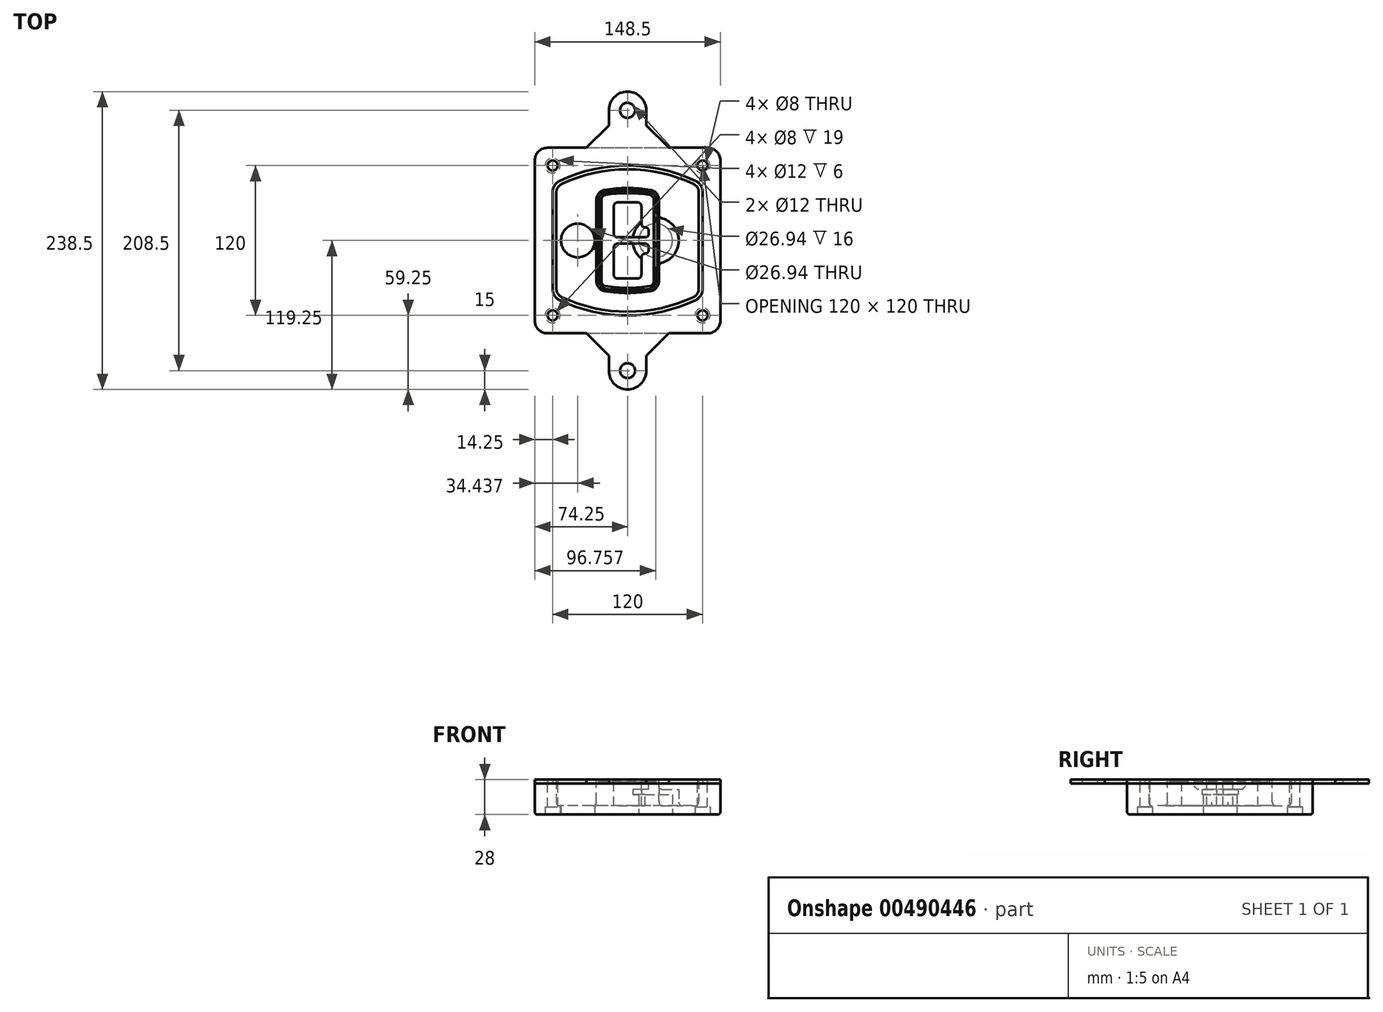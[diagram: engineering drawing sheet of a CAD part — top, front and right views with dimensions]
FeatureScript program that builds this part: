
annotation { "Feature Type Name" : "Feature", "Feature Type Description" : "" }
export const myFeature = defineFeature(function(context is Context, id is Id, definition is map)
    precondition{}
    {
        {
            var Q0;
            Q0=qCreatedBy(makeId("Top.planeOp"),FACE);
            var sketch = newSketch(context, id + "F0", { "sketchPlane" : qUnion([Q0])});
            skPoint(sketch, "E0.rect.middle", {"position": v(0, 0) * mm});
            skLineSegment(sketch, "E1.bottom", {"start": v(-64.25, -74.25) * mm, "end": v(64.25, -74.25) * mm});
            skLineSegment(sketch, "E1.top", {"start": v(-64.25, 74.25) * mm, "end": v(64.25, 74.25) * mm});
            skLineSegment(sketch, "E1.left", {"start": v(-74.25, -64.25) * mm, "end": v(-74.25, 64.25) * mm});
            skLineSegment(sketch, "E1.right", {"start": v(74.25, -64.25) * mm, "end": v(74.25, 64.25) * mm});
            skLineSegment(sketch, "E2", {"start": v(-74.25, 74.25) * mm, "end": v(74.25, -74.25) * mm, "construction": true});
            skLineSegment(sketch, "E3", {"start": v(74.25, 74.25) * mm, "end": v(-74.25, -74.25) * mm, "construction": true});
            skCircle(sketch, "E4", {"center": v(-60, 60) * mm, "radius": 4 * mm});
            skCircle(sketch, "E5", {"center": v(60, 60) * mm, "radius": 4 * mm});
            skCircle(sketch, "E6", {"center": v(60, -60) * mm, "radius": 4 * mm});
            skCircle(sketch, "E7", {"center": v(-60, -60) * mm, "radius": 4 * mm});
            skLineSegment(sketch, "E8", {"start": v(-60, 60) * mm, "end": v(60, 60) * mm, "construction": true});
            skLineSegment(sketch, "E9", {"start": v(60, 60) * mm, "end": v(60, -60) * mm, "construction": true});
            skLineSegment(sketch, "E10", {"start": v(60, -60) * mm, "end": v(-60, -60) * mm, "construction": true});
            skLineSegment(sketch, "E11", {"start": v(-60, -60) * mm, "end": v(-60, 60) * mm, "construction": true});
            skLineSegment(sketch, "E12", {"start": v(-60, 38.83) * mm, "end": v(-60, -38.83) * mm});
            skLineSegment(sketch, "E13", {"start": v(60, 38.83) * mm, "end": v(60, -38.83) * mm});
            skArc(sketch, "E14", {"start": v(54.26, 47.88) * mm, "mid": v(0, 60) * mm, "end": v(-54.26, 47.88) * mm});
            skArc(sketch, "E15", {"start": v(-54.26, -47.88) * mm, "mid": v(0, -60) * mm, "end": v(54.26, -47.88) * mm});
            skLineSegment(sketch, "E16", {"start": v(-60, 0) * mm, "end": v(60, 0) * mm, "construction": true});
            skPoint(sketch, "E17.visualSharp", {"position": v(-60, -45) * mm});
            skArc(sketch, "E17.filletArc", {"start": v(-60, -38.83) * mm, "mid": v(-58.44, -44.2) * mm, "end": v(-54.26, -47.88) * mm});
            skPoint(sketch, "E18.visualSharp", {"position": v(-60, 45) * mm});
            skArc(sketch, "E18.filletArc", {"start": v(-54.26, 47.88) * mm, "mid": v(-58.44, 44.2) * mm, "end": v(-60, 38.83) * mm});
            skPoint(sketch, "E19.visualSharp", {"position": v(60, 45) * mm});
            skArc(sketch, "E19.filletArc", {"start": v(60, 38.83) * mm, "mid": v(58.44, 44.2) * mm, "end": v(54.26, 47.88) * mm});
            skPoint(sketch, "E20.visualSharp", {"position": v(60, -45) * mm});
            skArc(sketch, "E20.filletArc", {"start": v(54.26, -47.88) * mm, "mid": v(58.44, -44.2) * mm, "end": v(60, -38.83) * mm});
            skPoint(sketch, "E21.visualSharp", {"position": v(-74.25, 74.25) * mm});
            skArc(sketch, "E21.filletArc", {"start": v(-64.25, 74.25) * mm, "mid": v(-71.32, 71.32) * mm, "end": v(-74.25, 64.25) * mm});
            skPoint(sketch, "E22.visualSharp", {"position": v(74.25, 74.25) * mm});
            skArc(sketch, "E22.filletArc", {"start": v(74.25, 64.25) * mm, "mid": v(71.32, 71.32) * mm, "end": v(64.25, 74.25) * mm});
            skPoint(sketch, "E23.visualSharp", {"position": v(74.25, -74.25) * mm});
            skArc(sketch, "E23.filletArc", {"start": v(64.25, -74.25) * mm, "mid": v(71.32, -71.32) * mm, "end": v(74.25, -64.25) * mm});
            skPoint(sketch, "E24.visualSharp", {"position": v(-74.25, -74.25) * mm});
            skArc(sketch, "E24.filletArc", {"start": v(-74.25, -64.25) * mm, "mid": v(-71.32, -71.32) * mm, "end": v(-64.25, -74.25) * mm});
            skArc(sketch, "E25.0", {"start": v(57, 38.83) * mm, "mid": v(55.9, 42.58) * mm, "end": v(52.98, 45.17) * mm});
            skLineSegment(sketch, "E25.1", {"start": v(57, 38.83) * mm, "end": v(57, -38.83) * mm});
            skArc(sketch, "E25.2", {"start": v(52.98, -45.17) * mm, "mid": v(55.9, -42.58) * mm, "end": v(57, -38.83) * mm});
            skArc(sketch, "E25.3", {"start": v(-52.98, -45.17) * mm, "mid": v(0, -57) * mm, "end": v(52.98, -45.17) * mm});
            skArc(sketch, "E25.4", {"start": v(-57, -38.83) * mm, "mid": v(-55.9, -42.58) * mm, "end": v(-52.98, -45.17) * mm});
            skArc(sketch, "E25.5", {"start": v(52.98, 45.17) * mm, "mid": v(0, 57) * mm, "end": v(-52.98, 45.17) * mm});
            skLineSegment(sketch, "E25.6", {"start": v(-57, 38.83) * mm, "end": v(-57, -38.83) * mm});
            skArc(sketch, "E25.7", {"start": v(-52.98, 45.17) * mm, "mid": v(-55.9, 42.58) * mm, "end": v(-57, 38.83) * mm});
            skArc(sketch, "E26.0", {"start": v(-55.96, 51.5) * mm, "mid": v(-61.82, 46.33) * mm, "end": v(-64, 38.83) * mm});
            skArc(sketch, "E26.1", {"start": v(55.96, 51.5) * mm, "mid": v(0, 64) * mm, "end": v(-55.96, 51.5) * mm});
            skArc(sketch, "E26.2", {"start": v(64, 38.83) * mm, "mid": v(61.82, 46.33) * mm, "end": v(55.96, 51.5) * mm});
            skLineSegment(sketch, "E26.3", {"start": v(64, 38.83) * mm, "end": v(64, -38.83) * mm});
            skArc(sketch, "E26.4", {"start": v(55.96, -51.5) * mm, "mid": v(61.82, -46.33) * mm, "end": v(64, -38.83) * mm});
            skLineSegment(sketch, "E26.5", {"start": v(-64, 38.83) * mm, "end": v(-64, -38.83) * mm});
            skArc(sketch, "E26.6", {"start": v(-55.96, -51.5) * mm, "mid": v(0, -64) * mm, "end": v(55.96, -51.5) * mm});
            skArc(sketch, "E26.7", {"start": v(-64, -38.83) * mm, "mid": v(-61.82, -46.33) * mm, "end": v(-55.96, -51.5) * mm});
            skSolve(sketch);
        }
        {
            var Q0;
            Q0=makeQuery(id+"F0.imprint","IMPRINT",FACE,{"disambiguationData":[TD([[makeQuery(id+"F0.imprint","IMPRINT",EDGE,{"derivedFrom":sQuery(id+"F0.wireOp",EDGE,"E1.bottom")}),1.0]])]});
            var Q1;
            Q1=makeQuery(id+"F0.imprint","IMPRINT",FACE,{"disambiguationData":[TD([[makeQuery(id+"F0.imprint","IMPRINT",EDGE,{"derivedFrom":sQuery(id+"F0.wireOp",EDGE,"E12")}),1.0]])]});
            var Q2;
            Q2=makeQuery(id+"F0.imprint","IMPRINT",FACE,{"disambiguationData":[TD([[makeQuery(id+"F0.imprint","IMPRINT",EDGE,{"derivedFrom":sQuery(id+"F0.wireOp",EDGE,"E25.0")}),1.0]])]});
            var Q3;
            Q3=makeQuery(id+"F0.imprint","IMPRINT",FACE,{"disambiguationData":[TD([[makeQuery(id+"F0.imprint","IMPRINT",EDGE,{"derivedFrom":sQuery(id+"F0.wireOp",EDGE,"E12")}),-1.0]])]});
            extrude(context, id + "F1", {"entities" : qUnion([Q0, Q1, Q2, Q3]), "oppositeDirection" : true, "depth" : 25 * mm});
        }
        {
            var Q0;
            Q0=makeQuery(id+"F0.imprint","IMPRINT",FACE,{"disambiguationData":[TD([[makeQuery(id+"F0.imprint","IMPRINT",EDGE,{"derivedFrom":sQuery(id+"F0.wireOp",EDGE,"E12")}),1.0]])]});
            extrude(context, id + "F2", {"entities" : qUnion([Q0]), "operationType" : NewBodyOperationType.ADD, "depth" : 3 * mm});
        }
        {
            var Q0;
            Q0=makeQuery(id+"F0.imprint","IMPRINT",FACE,{"disambiguationData":[TD([[makeQuery(id+"F0.imprint","IMPRINT",EDGE,{"derivedFrom":sQuery(id+"F0.wireOp",EDGE,"E25.0")}),1.0]])]});
            extrude(context, id + "F3", {"entities" : qUnion([Q0]), "operationType" : NewBodyOperationType.REMOVE, "oppositeDirection" : true, "depth" : 18 * mm});
        }
        {
            var Q0;
            Q0=makeQuery(id+"F2.opExtrude","CAP_FACE",FACE,{"disambiguationData":[OSD([sQuery(id+"F0.wireOp",EDGE,"E12"),sQuery(id+"F0.wireOp",EDGE,"E13"),sQuery(id+"F0.wireOp",EDGE,"E14"),sQuery(id+"F0.wireOp",EDGE,"E15"),sQuery(id+"F0.wireOp",EDGE,"E17.filletArc"),sQuery(id+"F0.wireOp",EDGE,"E18.filletArc"),sQuery(id+"F0.wireOp",EDGE,"E19.filletArc"),sQuery(id+"F0.wireOp",EDGE,"E20.filletArc"),sQuery(id+"F0.wireOp",EDGE,"E25.0"),sQuery(id+"F0.wireOp",EDGE,"E25.1"),sQuery(id+"F0.wireOp",EDGE,"E25.2"),sQuery(id+"F0.wireOp",EDGE,"E25.3"),sQuery(id+"F0.wireOp",EDGE,"E25.4"),sQuery(id+"F0.wireOp",EDGE,"E25.5"),sQuery(id+"F0.wireOp",EDGE,"E25.6"),sQuery(id+"F0.wireOp",EDGE,"E25.7")])],"isStart":false});
            var sketch = newSketch(context, id + "F4", { "sketchPlane" : qUnion([Q0])});
            skArc(sketch, "E27.0", {"start": v(-18.34, -40.45) * mm, "mid": v(0, -42) * mm, "end": v(18.34, -40.45) * mm});
            skArc(sketch, "E28.0", {"start": v(18.34, 40.45) * mm, "mid": v(0, 42) * mm, "end": v(-18.34, 40.45) * mm});
            skLineSegment(sketch, "E29", {"start": v(-25, 32.57) * mm, "end": v(-25, -32.57) * mm});
            skLineSegment(sketch, "E30", {"start": v(25, 32.57) * mm, "end": v(25, -32.57) * mm});
            skLineSegment(sketch, "E31", {"start": v(-25, 39.1) * mm, "end": v(25, 39.1) * mm, "construction": true});
            skLineSegment(sketch, "E32", {"start": v(-25, -39.1) * mm, "end": v(25, -39.1) * mm, "construction": true});
            skPoint(sketch, "E33.visualSharp", {"position": v(-25, 39.1) * mm});
            skArc(sketch, "E33.filletArc", {"start": v(-18.34, 40.45) * mm, "mid": v(-23.11, 37.73) * mm, "end": v(-25, 32.57) * mm});
            skPoint(sketch, "E34.visualSharp", {"position": v(25, 39.1) * mm});
            skArc(sketch, "E34.filletArc", {"start": v(25, 32.57) * mm, "mid": v(23.11, 37.73) * mm, "end": v(18.34, 40.45) * mm});
            skPoint(sketch, "E35.visualSharp", {"position": v(25, -39.1) * mm});
            skArc(sketch, "E35.filletArc", {"start": v(18.34, -40.45) * mm, "mid": v(23.11, -37.73) * mm, "end": v(25, -32.57) * mm});
            skPoint(sketch, "E36.visualSharp", {"position": v(-25, -39.1) * mm});
            skArc(sketch, "E36.filletArc", {"start": v(-25, -32.57) * mm, "mid": v(-23.11, -37.73) * mm, "end": v(-18.34, -40.45) * mm});
            skArc(sketch, "E37.0", {"start": v(52.98, 45.17) * mm, "mid": v(0, 57) * mm, "end": v(-52.98, 45.17) * mm});
            skArc(sketch, "E37.1", {"start": v(-52.98, 45.17) * mm, "mid": v(-55.9, 42.58) * mm, "end": v(-57, 38.83) * mm});
            skLineSegment(sketch, "E37.2", {"start": v(-57, 38.83) * mm, "end": v(-57, -38.83) * mm});
            skArc(sketch, "E37.3", {"start": v(-57, -38.83) * mm, "mid": v(-55.9, -42.58) * mm, "end": v(-52.98, -45.17) * mm});
            skArc(sketch, "E37.4", {"start": v(-52.98, -45.17) * mm, "mid": v(0, -57) * mm, "end": v(52.98, -45.17) * mm});
            skArc(sketch, "E37.5", {"start": v(52.98, -45.17) * mm, "mid": v(55.9, -42.58) * mm, "end": v(57, -38.83) * mm});
            skLineSegment(sketch, "E37.6", {"start": v(57, 38.83) * mm, "end": v(57, -38.83) * mm});
            skArc(sketch, "E37.7", {"start": v(57, 38.83) * mm, "mid": v(55.9, 42.58) * mm, "end": v(52.98, 45.17) * mm});
            skLineSegment(sketch, "E38.0", {"start": v(23, 32.57) * mm, "end": v(23, -32.57) * mm});
            skArc(sketch, "E38.1", {"start": v(18, -38.48) * mm, "mid": v(21.58, -36.44) * mm, "end": v(23, -32.57) * mm});
            skArc(sketch, "E38.2", {"start": v(-18, -38.48) * mm, "mid": v(0, -40) * mm, "end": v(18, -38.48) * mm});
            skArc(sketch, "E38.3", {"start": v(-23, -32.57) * mm, "mid": v(-21.58, -36.44) * mm, "end": v(-18, -38.48) * mm});
            skLineSegment(sketch, "E38.4", {"start": v(-23, 32.57) * mm, "end": v(-23, -32.57) * mm});
            skArc(sketch, "E38.5", {"start": v(23, 32.57) * mm, "mid": v(21.58, 36.44) * mm, "end": v(18, 38.48) * mm});
            skArc(sketch, "E38.6", {"start": v(-18, 38.48) * mm, "mid": v(-21.58, 36.44) * mm, "end": v(-23, 32.57) * mm});
            skArc(sketch, "E38.7", {"start": v(18, 38.48) * mm, "mid": v(0, 40) * mm, "end": v(-18, 38.48) * mm});
            skArc(sketch, "E39.0", {"start": v(21, 32.57) * mm, "mid": v(20.06, 35.15) * mm, "end": v(17.67, 36.5) * mm});
            skLineSegment(sketch, "E39.1", {"start": v(21, 32.57) * mm, "end": v(21, -32.57) * mm});
            skArc(sketch, "E39.2", {"start": v(17.67, -36.5) * mm, "mid": v(20.06, -35.15) * mm, "end": v(21, -32.57) * mm});
            skArc(sketch, "E39.3", {"start": v(-17.67, -36.5) * mm, "mid": v(0, -38) * mm, "end": v(17.67, -36.5) * mm});
            skArc(sketch, "E39.4", {"start": v(-21, -32.57) * mm, "mid": v(-20.06, -35.15) * mm, "end": v(-17.67, -36.5) * mm});
            skArc(sketch, "E39.5", {"start": v(17.67, 36.5) * mm, "mid": v(0, 38) * mm, "end": v(-17.67, 36.5) * mm});
            skLineSegment(sketch, "E39.6", {"start": v(-21, 32.57) * mm, "end": v(-21, -32.57) * mm});
            skArc(sketch, "E39.7", {"start": v(-17.67, 36.5) * mm, "mid": v(-20.06, 35.15) * mm, "end": v(-21, 32.57) * mm});
            skLineSegment(sketch, "E40", {"start": v(-25, 0) * mm, "end": v(25, 0) * mm, "construction": true});
            skLineSegment(sketch, "E41", {"start": v(-11, 5.5) * mm, "end": v(-11, 27.5) * mm});
            skLineSegment(sketch, "E42", {"start": v(-8, 30.5) * mm, "end": v(8, 30.5) * mm});
            skLineSegment(sketch, "E43", {"start": v(11, 27.5) * mm, "end": v(11, 13.5) * mm});
            skLineSegment(sketch, "E44", {"start": v(14, 10.5) * mm, "end": v(14, 10.5) * mm});
            skLineSegment(sketch, "E45", {"start": v(17, 7.5) * mm, "end": v(17, 5.5) * mm});
            skLineSegment(sketch, "E46", {"start": v(14, 2.5) * mm, "end": v(-8, 2.5) * mm});
            skPoint(sketch, "E47.visualSharp", {"position": v(-11, 30.5) * mm});
            skArc(sketch, "E47.filletArc", {"start": v(-8, 30.5) * mm, "mid": v(-10.12, 29.62) * mm, "end": v(-11, 27.5) * mm});
            skPoint(sketch, "E48.visualSharp", {"position": v(11, 30.5) * mm});
            skArc(sketch, "E48.filletArc", {"start": v(11, 27.5) * mm, "mid": v(10.12, 29.62) * mm, "end": v(8, 30.5) * mm});
            skPoint(sketch, "E49.visualSharp", {"position": v(11, 10.5) * mm});
            skArc(sketch, "E49.filletArc", {"start": v(11, 13.5) * mm, "mid": v(11.88, 11.38) * mm, "end": v(14, 10.5) * mm});
            skPoint(sketch, "E50.visualSharp", {"position": v(17, 10.5) * mm});
            skArc(sketch, "E50.filletArc", {"start": v(17, 7.5) * mm, "mid": v(16.12, 9.62) * mm, "end": v(14, 10.5) * mm});
            skPoint(sketch, "E51.visualSharp", {"position": v(17, 2.5) * mm});
            skArc(sketch, "E51.filletArc", {"start": v(14, 2.5) * mm, "mid": v(16.12, 3.38) * mm, "end": v(17, 5.5) * mm});
            skPoint(sketch, "E52.visualSharp", {"position": v(-11, 2.5) * mm});
            skArc(sketch, "E52.filletArc", {"start": v(-11, 5.5) * mm, "mid": v(-10.12, 3.38) * mm, "end": v(-8, 2.5) * mm});
            skLineSegment(sketch, "E53.0.MirrorCS", {"start": v(14, -2.5) * mm, "end": v(-8, -2.5) * mm});
            skArc(sketch, "E54.0.MirrorCS", {"start": v(-11, -5.5) * mm, "mid": v(-10.12, -3.38) * mm, "end": v(-8, -2.5) * mm});
            skLineSegment(sketch, "E55.0.MirrorCS", {"start": v(-11, -5.5) * mm, "end": v(-11, -27.5) * mm});
            skArc(sketch, "E56.0.MirrorCS", {"start": v(-8, -30.5) * mm, "mid": v(-10.12, -29.62) * mm, "end": v(-11, -27.5) * mm});
            skLineSegment(sketch, "E57.0.MirrorCS", {"start": v(-8, -30.5) * mm, "end": v(8, -30.5) * mm});
            skArc(sketch, "E58.0.MirrorCS", {"start": v(11, -27.5) * mm, "mid": v(10.12, -29.62) * mm, "end": v(8, -30.5) * mm});
            skLineSegment(sketch, "E59.0.MirrorCS", {"start": v(11, -27.5) * mm, "end": v(11, -13.5) * mm});
            skArc(sketch, "E60.0.MirrorCS", {"start": v(11, -13.5) * mm, "mid": v(11.88, -11.38) * mm, "end": v(14, -10.5) * mm});
            skArc(sketch, "E61.0.MirrorCS", {"start": v(17, -7.5) * mm, "mid": v(16.12, -9.62) * mm, "end": v(14, -10.5) * mm});
            skLineSegment(sketch, "E62.0.MirrorCS", {"start": v(17, -7.5) * mm, "end": v(17, -5.5) * mm});
            skArc(sketch, "E63.0.MirrorCS", {"start": v(14, -2.5) * mm, "mid": v(16.12, -3.38) * mm, "end": v(17, -5.5) * mm});
            skSolve(sketch);
        }
        {
            var Q0;
            Q0=makeQuery(id+"F4.imprint","IMPRINT",FACE,{"disambiguationData":[TD([[makeQuery(id+"F4.imprint","IMPRINT",EDGE,{"derivedFrom":sQuery(id+"F4.wireOp",EDGE,"E27.0")}),1.0]])]});
            var Q1;
            Q1=makeQuery(id+"F4.imprint","IMPRINT",FACE,{"disambiguationData":[TD([[makeQuery(id+"F4.imprint","IMPRINT",EDGE,{"derivedFrom":sQuery(id+"F4.wireOp",EDGE,"E38.0")}),-1.0]])]});
            var Q2;
            Q2=makeQuery(id+"F4.imprint","IMPRINT",FACE,{"disambiguationData":[TD([[makeQuery(id+"F4.imprint","IMPRINT",EDGE,{"derivedFrom":sQuery(id+"F4.wireOp",EDGE,"E39.0")}),1.0]])]});
            extrude(context, id + "F5", {"entities" : qUnion([Q0, Q1, Q2]), "operationType" : NewBodyOperationType.ADD, "endBound" : BoundingType.UP_TO_NEXT, "oppositeDirection" : true, "depth" : 25 * mm});
        }
        {
            var Q0;
            Q0=makeQuery(id+"F4.imprint","IMPRINT",FACE,{"disambiguationData":[TD([[makeQuery(id+"F4.imprint","IMPRINT",EDGE,{"derivedFrom":sQuery(id+"F4.wireOp",EDGE,"E38.0")}),-1.0]])]});
            extrude(context, id + "F6", {"entities" : qUnion([Q0]), "operationType" : NewBodyOperationType.REMOVE, "oppositeDirection" : true, "depth" : 2 * mm});
        }
        {
            var Q0;
            Q0=makeQuery(id+"F1.opExtrude","CAP_FACE",FACE,{"disambiguationData":[OSD([sQuery(id+"F0.wireOp",EDGE,"E1.bottom"),sQuery(id+"F0.wireOp",EDGE,"E1.top"),sQuery(id+"F0.wireOp",EDGE,"E1.left"),sQuery(id+"F0.wireOp",EDGE,"E1.right"),sQuery(id+"F0.wireOp",EDGE,"E4"),sQuery(id+"F0.wireOp",EDGE,"E5"),sQuery(id+"F0.wireOp",EDGE,"E6"),sQuery(id+"F0.wireOp",EDGE,"E7"),sQuery(id+"F0.wireOp",EDGE,"E21.filletArc"),sQuery(id+"F0.wireOp",EDGE,"E22.filletArc"),sQuery(id+"F0.wireOp",EDGE,"E23.filletArc"),sQuery(id+"F0.wireOp",EDGE,"E24.filletArc")])],"isStart":false});
            var sketch = newSketch(context, id + "F7", { "sketchPlane" : qUnion([Q0])});
            skCircle(sketch, "E64", {"center": v(22.5, 0) * mm, "radius": 13.47 * mm});
            skCircle(sketch, "E65", {"center": v(-39.81, 0) * mm, "radius": 13.47 * mm});
            skLineSegment(sketch, "E66", {"start": v(74.25, 0) * mm, "end": v(-74.25, 0) * mm});
            skCircle(sketch, "E67", {"center": v(22.5, 0) * mm, "radius": 18.47 * mm});
            skCircle(sketch, "E68", {"center": v(60, -60) * mm, "radius": 6 * mm});
            skCircle(sketch, "E69", {"center": v(-60, -60) * mm, "radius": 6 * mm});
            skCircle(sketch, "E70", {"center": v(-60, 60) * mm, "radius": 6 * mm});
            skCircle(sketch, "E71", {"center": v(60, 60) * mm, "radius": 6 * mm});
            skSolve(sketch);
        }
        {
            var Q0;
            {var subQ1=sQuery(id+"F7.wireOp",EDGE,"E66");var subQ4=sQuery(id+"F7.wireOp",EDGE,"E64");var subQ6=makeQuery(id+"F7.imprint","INTERSECT",VERTEX,{"disambiguationData":[OD(0.0)],"derivedFrom":[subQ4,subQ1]});Q0=makeQuery(id+"F7.imprint","IMPRINT",FACE,{"disambiguationData":[TD([[makeQuery(id+"F7.imprint","IMPRINT",EDGE,{"disambiguationData":[TD([[subQ6,-1.0]])],"derivedFrom":subQ4}),-1.0]])]});}
            var Q1;
            {var subQ0=sQuery(id+"F7.wireOp",EDGE,"E66");var subQ1=sQuery(id+"F7.wireOp",EDGE,"E64");var subQ3=makeQuery(id+"F7.imprint","INTERSECT",VERTEX,{"disambiguationData":[OD(0.0)],"derivedFrom":[subQ1,subQ0]});Q1=makeQuery(id+"F7.imprint","IMPRINT",FACE,{"disambiguationData":[TD([[makeQuery(id+"F7.imprint","IMPRINT",EDGE,{"disambiguationData":[TD([[subQ3,-1.0]])],"derivedFrom":subQ1}),1.0]])]});}
            var Q2;
            {var subQ0=sQuery(id+"F7.wireOp",EDGE,"E66");var subQ1=sQuery(id+"F7.wireOp",EDGE,"E64");var subQ3=makeQuery(id+"F7.imprint","INTERSECT",VERTEX,{"disambiguationData":[OD(0.0)],"derivedFrom":[subQ1,subQ0]});Q2=makeQuery(id+"F7.imprint","IMPRINT",FACE,{"disambiguationData":[TD([[makeQuery(id+"F7.imprint","IMPRINT",EDGE,{"disambiguationData":[TD([[subQ3,1.0]])],"derivedFrom":subQ1}),1.0]])]});}
            var Q3;
            {var subQ1=sQuery(id+"F7.wireOp",EDGE,"E66");var subQ4=sQuery(id+"F7.wireOp",EDGE,"E64");var subQ6=makeQuery(id+"F7.imprint","INTERSECT",VERTEX,{"disambiguationData":[OD(0.0)],"derivedFrom":[subQ4,subQ1]});Q3=makeQuery(id+"F7.imprint","IMPRINT",FACE,{"disambiguationData":[TD([[makeQuery(id+"F7.imprint","IMPRINT",EDGE,{"disambiguationData":[TD([[subQ6,1.0]])],"derivedFrom":subQ4}),-1.0]])]});}
            extrude(context, id + "F8", {"entities" : qUnion([Q0, Q1, Q2, Q3]), "operationType" : NewBodyOperationType.ADD, "oppositeDirection" : true, "depth" : 20 * mm});
        }
        {
            var Q0;
            {var subQ0=sQuery(id+"F7.wireOp",EDGE,"E66");var subQ1=sQuery(id+"F7.wireOp",EDGE,"E64");var subQ3=makeQuery(id+"F7.imprint","INTERSECT",VERTEX,{"disambiguationData":[OD(0.0)],"derivedFrom":[subQ1,subQ0]});Q0=makeQuery(id+"F7.imprint","IMPRINT",FACE,{"disambiguationData":[TD([[makeQuery(id+"F7.imprint","IMPRINT",EDGE,{"disambiguationData":[TD([[subQ3,-1.0]])],"derivedFrom":subQ1}),1.0]])]});}
            var Q1;
            {var subQ0=sQuery(id+"F7.wireOp",EDGE,"E66");var subQ1=sQuery(id+"F7.wireOp",EDGE,"E64");var subQ3=makeQuery(id+"F7.imprint","INTERSECT",VERTEX,{"disambiguationData":[OD(0.0)],"derivedFrom":[subQ1,subQ0]});Q1=makeQuery(id+"F7.imprint","IMPRINT",FACE,{"disambiguationData":[TD([[makeQuery(id+"F7.imprint","IMPRINT",EDGE,{"disambiguationData":[TD([[subQ3,1.0]])],"derivedFrom":subQ1}),1.0]])]});}
            extrude(context, id + "F9", {"entities" : qUnion([Q0, Q1]), "operationType" : NewBodyOperationType.REMOVE, "oppositeDirection" : true, "depth" : 16 * mm});
        }
        {
            var Q0;
            {var subQ0=sQuery(id+"F7.wireOp",EDGE,"E66");var subQ1=sQuery(id+"F7.wireOp",EDGE,"E65");var subQ3=makeQuery(id+"F7.imprint","INTERSECT",VERTEX,{"disambiguationData":[OD(0.0)],"derivedFrom":[subQ1,subQ0]});Q0=makeQuery(id+"F7.imprint","IMPRINT",FACE,{"disambiguationData":[TD([[makeQuery(id+"F7.imprint","IMPRINT",EDGE,{"disambiguationData":[TD([[subQ3,-1.0]])],"derivedFrom":subQ1}),1.0]])]});}
            var Q1;
            {var subQ0=sQuery(id+"F7.wireOp",EDGE,"E66");var subQ1=sQuery(id+"F7.wireOp",EDGE,"E65");var subQ3=makeQuery(id+"F7.imprint","INTERSECT",VERTEX,{"disambiguationData":[OD(0.0)],"derivedFrom":[subQ1,subQ0]});Q1=makeQuery(id+"F7.imprint","IMPRINT",FACE,{"disambiguationData":[TD([[makeQuery(id+"F7.imprint","IMPRINT",EDGE,{"disambiguationData":[TD([[subQ3,1.0]])],"derivedFrom":subQ1}),1.0]])]});}
            extrude(context, id + "F10", {"entities" : qUnion([Q0, Q1]), "operationType" : NewBodyOperationType.REMOVE, "oppositeDirection" : true, "depth" : 25 * mm});
        }
        {
            var Q0;
            Q0=makeQuery(id+"F7.imprint","IMPRINT",FACE,{"disambiguationData":[TD([[makeQuery(id+"F7.imprint","IMPRINT",EDGE,{"derivedFrom":sQuery(id+"F7.wireOp",EDGE,"E68")}),1.0]])]});
            var Q1;
            Q1=makeQuery(id+"F7.imprint","IMPRINT",FACE,{"disambiguationData":[TD([[makeQuery(id+"F7.imprint","IMPRINT",EDGE,{"derivedFrom":makeQuery(id+"F1.opExtrude","CAP_EDGE",EDGE,{"disambiguationData":[OSD([sQuery(id+"F0.wireOp",EDGE,"E5")])],"isStart":false})}),-1.0]])]});
            var Q2;
            Q2=makeQuery(id+"F7.imprint","IMPRINT",FACE,{"disambiguationData":[TD([[makeQuery(id+"F7.imprint","IMPRINT",EDGE,{"derivedFrom":sQuery(id+"F7.wireOp",EDGE,"E69")}),1.0]])]});
            var Q3;
            Q3=makeQuery(id+"F7.imprint","IMPRINT",FACE,{"disambiguationData":[TD([[makeQuery(id+"F7.imprint","IMPRINT",EDGE,{"derivedFrom":makeQuery(id+"F1.opExtrude","CAP_EDGE",EDGE,{"disambiguationData":[OSD([sQuery(id+"F0.wireOp",EDGE,"E4")])],"isStart":false})}),-1.0]])]});
            var Q4;
            Q4=makeQuery(id+"F7.imprint","IMPRINT",FACE,{"disambiguationData":[TD([[makeQuery(id+"F7.imprint","IMPRINT",EDGE,{"derivedFrom":sQuery(id+"F7.wireOp",EDGE,"E70")}),1.0]])]});
            var Q5;
            Q5=makeQuery(id+"F7.imprint","IMPRINT",FACE,{"disambiguationData":[TD([[makeQuery(id+"F7.imprint","IMPRINT",EDGE,{"derivedFrom":makeQuery(id+"F1.opExtrude","CAP_EDGE",EDGE,{"disambiguationData":[OSD([sQuery(id+"F0.wireOp",EDGE,"E7")])],"isStart":false})}),-1.0]])]});
            var Q6;
            Q6=makeQuery(id+"F7.imprint","IMPRINT",FACE,{"disambiguationData":[TD([[makeQuery(id+"F7.imprint","IMPRINT",EDGE,{"derivedFrom":sQuery(id+"F7.wireOp",EDGE,"E71")}),1.0]])]});
            var Q7;
            Q7=makeQuery(id+"F7.imprint","IMPRINT",FACE,{"disambiguationData":[TD([[makeQuery(id+"F7.imprint","IMPRINT",EDGE,{"derivedFrom":makeQuery(id+"F1.opExtrude","CAP_EDGE",EDGE,{"disambiguationData":[OSD([sQuery(id+"F0.wireOp",EDGE,"E6")])],"isStart":false})}),-1.0]])]});
            extrude(context, id + "F11", {"entities" : qUnion([Q0, Q1, Q2, Q3, Q4, Q5, Q6, Q7]), "operationType" : NewBodyOperationType.REMOVE, "oppositeDirection" : true, "depth" : 6 * mm});
        }
        {
            var Q0;
            Q0=makeQuery(id+"F9.boolean.opBoolean","COPY",FACE,{"derivedFrom":makeQuery(id+"F9.opExtrude","CAP_FACE",FACE,{"disambiguationData":[OSD([sQuery(id+"F7.wireOp",EDGE,"E64")])],"isStart":false})});
            var sketch = newSketch(context, id + "F12", { "sketchPlane" : qUnion([Q0])});
            skArc(sketch, "E72.0", {"start": v(11, 14.45) * mm, "mid": v(6.45, 9.13) * mm, "end": v(4.2, 2.5) * mm});
            skArc(sketch, "E72.1", {"start": v(4.2, -2.5) * mm, "mid": v(6.45, -9.13) * mm, "end": v(11, -14.45) * mm});
            skLineSegment(sketch, "E73", {"start": v(4.2, -2.5) * mm, "end": v(14, -2.5) * mm});
            skLineSegment(sketch, "E74.0", {"start": v(14, 2.5) * mm, "end": v(4.2, 2.5) * mm});
            skArc(sketch, "E74.1", {"start": v(14, 2.5) * mm, "mid": v(16.12, 3.38) * mm, "end": v(17, 5.5) * mm});
            skLineSegment(sketch, "E74.2", {"start": v(17, 7.5) * mm, "end": v(17, 5.5) * mm});
            skArc(sketch, "E74.3", {"start": v(17, 7.5) * mm, "mid": v(16.12, 9.62) * mm, "end": v(14, 10.5) * mm});
            skArc(sketch, "E74.4", {"start": v(11, 13.5) * mm, "mid": v(11.88, 11.38) * mm, "end": v(14, 10.5) * mm});
            skLineSegment(sketch, "E74.5", {"start": v(11, 14.45) * mm, "end": v(11, 13.5) * mm});
            skLineSegment(sketch, "E74.7", {"start": v(14, -2.5) * mm, "end": v(4.2, -2.5) * mm});
            skArc(sketch, "E74.8", {"start": v(14, -2.5) * mm, "mid": v(16.12, -3.38) * mm, "end": v(17, -5.5) * mm});
            skLineSegment(sketch, "E74.9", {"start": v(17, -7.5) * mm, "end": v(17, -5.5) * mm});
            skArc(sketch, "E74.10", {"start": v(17, -7.5) * mm, "mid": v(16.12, -9.62) * mm, "end": v(14, -10.5) * mm});
            skArc(sketch, "E74.11", {"start": v(11, -13.5) * mm, "mid": v(11.88, -11.38) * mm, "end": v(14, -10.5) * mm});
            skLineSegment(sketch, "E74.12", {"start": v(11, -14.45) * mm, "end": v(11, -13.5) * mm});
            skPoint(sketch, "E75.orphan", {"position": v(11, -27.5) * mm});
            skPoint(sketch, "E76.orphan", {"position": v(-8, -2.5) * mm});
            skPoint(sketch, "E77.orphan", {"position": v(-8, 2.5) * mm});
            skPoint(sketch, "E78.orphan", {"position": v(11, 27.5) * mm});
            skSolve(sketch);
        }
        {
            var Q0;
            {var subQ7=sQuery(id+"F12.wireOp",EDGE,"E72.0");var subQ14=sQuery(id+"F12.wireOp",EDGE,"E72.1");var subQ16=sQuery(id+"F12.wireOp",EDGE,"E74.1");var subQ18=sQuery(id+"F12.wireOp",EDGE,"E74.8");Q0=qUnion([makeQuery(id+"F12.imprint","IMPRINT",FACE,{"disambiguationData":[TD([[makeQuery(id+"F12.imprint","IMPRINT",EDGE,{"derivedFrom":subQ7}),1.0]])]}),makeQuery(id+"F12.imprint","IMPRINT",FACE,{"disambiguationData":[TD([[makeQuery(id+"F12.imprint","IMPRINT",EDGE,{"derivedFrom":subQ14}),1.0]])]}),makeQuery(id+"F12.imprint","IMPRINT",FACE,{"disambiguationData":[TD([[makeQuery(id+"F12.imprint","IMPRINT",EDGE,{"derivedFrom":subQ16}),1.0]])]}),makeQuery(id+"F12.imprint","IMPRINT",FACE,{"disambiguationData":[TD([[makeQuery(id+"F12.imprint","IMPRINT",EDGE,{"derivedFrom":subQ18}),-1.0]])]})]);}
            var Q1;
            Q1=makeQuery(id+"F5.boolean.opBoolean","SPLIT",FACE,{"disambiguationData":[TD([makeQuery(id+"F5.opExtrude","SWEPT_FACE",FACE,{"disambiguationData":[OSD([sQuery(id+"F4.wireOp",EDGE,"E41")])]})])],"derivedFrom":makeQuery(id+"F3.boolean.opBoolean","COPY",FACE,{"derivedFrom":makeQuery(id+"F3.opExtrude","CAP_FACE",FACE,{"disambiguationData":[OSD([sQuery(id+"F0.wireOp",EDGE,"E25.0"),sQuery(id+"F0.wireOp",EDGE,"E25.1"),sQuery(id+"F0.wireOp",EDGE,"E25.2"),sQuery(id+"F0.wireOp",EDGE,"E25.3"),sQuery(id+"F0.wireOp",EDGE,"E25.4"),sQuery(id+"F0.wireOp",EDGE,"E25.5"),sQuery(id+"F0.wireOp",EDGE,"E25.6"),sQuery(id+"F0.wireOp",EDGE,"E25.7")])],"isStart":false})})});
            extrude(context, id + "F13", {"entities" : qUnion([Q0]), "operationType" : NewBodyOperationType.REMOVE, "endBound" : BoundingType.UP_TO_SURFACE, "endBoundEntityFace" : qUnion([Q1]), "depth" : 25 * mm});
        }
        {
            var Q0;
            Q0=makeQuery(id+"F3.boolean.opBoolean","COPY",EDGE,{"derivedFrom":makeQuery(id+"F3.opExtrude","CAP_EDGE",EDGE,{"disambiguationData":[OSD([sQuery(id+"F0.wireOp",EDGE,"E25.6")])],"isStart":false})});
            var Q1;
            Q1=makeQuery(id+"F8.boolean.opBoolean","INTERSECT",EDGE,{"derivedFrom":[makeQuery(id+"F5.opExtrude","SWEPT_FACE",FACE,{"disambiguationData":[OSD([sQuery(id+"F4.wireOp",EDGE,"E30")])]}),makeQuery(id+"F8.opExtrude","CAP_FACE",FACE,{"disambiguationData":[OSD([sQuery(id+"F7.wireOp",EDGE,"E67")])],"isStart":false})]});
            var Q2;
            Q2=makeQuery(id+"F8.boolean.opBoolean","INTERSECT",EDGE,{"disambiguationData":[OD(1.0)],"derivedFrom":[makeQuery(id+"F5.opExtrude","SWEPT_FACE",FACE,{"disambiguationData":[OSD([sQuery(id+"F4.wireOp",EDGE,"E30")])]}),makeQuery(id+"F8.opExtrude","SWEPT_FACE",FACE,{"disambiguationData":[OSD([sQuery(id+"F7.wireOp",EDGE,"E67")])]})]});
            var Q3;
            {var subQ0=sQuery(id+"F4.wireOp",EDGE,"E30");Q3=makeQuery(id+"F8.boolean.opBoolean","SPLIT",EDGE,{"disambiguationData":[TD([makeQuery(id+"F5.opExtrude","SWEPT_FACE",FACE,{"disambiguationData":[OSD([sQuery(id+"F4.wireOp",EDGE,"E35.filletArc")])]})])],"derivedFrom":makeQuery(id+"F5.opExtrude","CAP_EDGE",EDGE,{"disambiguationData":[OSD([subQ0])],"isStart":false})});}
            var Q4;
            {var subQ0=sQuery(id+"F0.wireOp",EDGE,"E25.7");var subQ1=sQuery(id+"F0.wireOp",EDGE,"E25.1");var subQ2=sQuery(id+"F0.wireOp",EDGE,"E25.6");var subQ3=sQuery(id+"F0.wireOp",EDGE,"E25.5");var subQ4=sQuery(id+"F0.wireOp",EDGE,"E25.4");var subQ5=sQuery(id+"F0.wireOp",EDGE,"E25.0");var subQ6=sQuery(id+"F0.wireOp",EDGE,"E25.2");var subQ7=sQuery(id+"F0.wireOp",EDGE,"E25.3");Q4=makeQuery(id+"F8.boolean.opBoolean","INTERSECT",EDGE,{"derivedFrom":[makeQuery(id+"F5.boolean.opBoolean","SPLIT",FACE,{"disambiguationData":[TD([makeQuery(id+"F2.opExtrude","SWEPT_FACE",FACE,{"disambiguationData":[OSD([subQ5])]})])],"derivedFrom":makeQuery(id+"F3.boolean.opBoolean","COPY",FACE,{"derivedFrom":makeQuery(id+"F3.opExtrude","CAP_FACE",FACE,{"disambiguationData":[OSD([subQ5,subQ1,subQ6,subQ7,subQ4,subQ3,subQ2,subQ0])],"isStart":false})})}),makeQuery(id+"F8.opExtrude","SWEPT_FACE",FACE,{"disambiguationData":[OSD([sQuery(id+"F7.wireOp",EDGE,"E67")])]})]});}
            var Q5;
            Q5=makeQuery(id+"F8.boolean.opBoolean","INTERSECT",EDGE,{"disambiguationData":[OD(0.0)],"derivedFrom":[makeQuery(id+"F5.opExtrude","SWEPT_FACE",FACE,{"disambiguationData":[OSD([sQuery(id+"F4.wireOp",EDGE,"E30")])]}),makeQuery(id+"F8.opExtrude","SWEPT_FACE",FACE,{"disambiguationData":[OSD([sQuery(id+"F7.wireOp",EDGE,"E67")])]})]});
            fillet(context, id + "F14", {"entities" : qUnion([Q0, Q1, Q2, Q3, Q4, Q5]), "radius" : 3 * mm, "tangentPropagation" : true, "allowEdgeOverflow" : false});
        }
        {
            var Q0;
            Q0=makeQuery(id+"F1.opExtrude","CAP_EDGE",EDGE,{"disambiguationData":[OSD([sQuery(id+"F0.wireOp",EDGE,"E1.bottom")])],"isStart":false});
            fillet(context, id + "F15", {"entities" : qUnion([Q0]), "radius" : 2 * mm, "tangentPropagation" : true, "allowEdgeOverflow" : false});
        }
        {
            var Q0;
            {var subQ0=sQuery(id+"F0.wireOp",EDGE,"E21.filletArc");var subQ1=sQuery(id+"F0.wireOp",EDGE,"E7");var subQ2=sQuery(id+"F0.wireOp",EDGE,"E6");var subQ3=sQuery(id+"F0.wireOp",EDGE,"E5");var subQ4=sQuery(id+"F0.wireOp",EDGE,"E4");var subQ5=sQuery(id+"F0.wireOp",EDGE,"E22.filletArc");var subQ6=sQuery(id+"F0.wireOp",EDGE,"E1.bottom");var subQ7=sQuery(id+"F0.wireOp",EDGE,"E1.right");var subQ8=sQuery(id+"F0.wireOp",EDGE,"E1.top");var subQ9=sQuery(id+"F0.wireOp",EDGE,"E1.left");var subQ10=sQuery(id+"F0.wireOp",EDGE,"E23.filletArc");var subQ11=sQuery(id+"F0.wireOp",EDGE,"E24.filletArc");Q0=makeQuery(id+"F2.boolean.opBoolean","SPLIT",FACE,{"disambiguationData":[TD([makeQuery(id+"F1.opExtrude","SWEPT_FACE",FACE,{"disambiguationData":[OSD([subQ6])]})])],"derivedFrom":makeQuery(id+"F1.opExtrude","CAP_FACE",FACE,{"disambiguationData":[OSD([subQ6,subQ8,subQ9,subQ7,subQ4,subQ3,subQ2,subQ1,subQ0,subQ5,subQ10,subQ11])],"isStart":true})});}
            var sketch = newSketch(context, id + "F16", { "sketchPlane" : qUnion([Q0])});
            skLineSegment(sketch, "E79", {"start": v(0, 74.25) * mm, "end": v(0, 104.25) * mm, "construction": true});
            skArc(sketch, "E80", {"start": v(15, 104.25) * mm, "mid": v(0, 119.25) * mm, "end": v(-15, 104.25) * mm});
            skLineSegment(sketch, "E81", {"start": v(15, 104.25) * mm, "end": v(15, 92.25) * mm});
            skLineSegment(sketch, "E82", {"start": v(-15, 104.25) * mm, "end": v(-15, 92.25) * mm});
            skLineSegment(sketch, "E83", {"start": v(-15, 92.25) * mm, "end": v(-33, 74.25) * mm});
            skLineSegment(sketch, "E84", {"start": v(15, 92.25) * mm, "end": v(33, 74.25) * mm});
            skCircle(sketch, "E85", {"center": v(0, 104.25) * mm, "radius": 6 * mm});
            skLineSegment(sketch, "E86", {"start": v(-74.25, 0) * mm, "end": v(74.25, 0) * mm, "construction": true});
            skLineSegment(sketch, "E87.MirrorCS", {"start": v(15, -104.25) * mm, "end": v(15, -92.25) * mm});
            skLineSegment(sketch, "E88.MirrorCS", {"start": v(-15, -104.25) * mm, "end": v(-15, -92.25) * mm});
            skLineSegment(sketch, "E89.MirrorCS", {"start": v(0, -74.25) * mm, "end": v(0, -104.25) * mm, "construction": true});
            skArc(sketch, "E90.MirrorCS", {"start": v(15, -104.25) * mm, "mid": v(0, -119.25) * mm, "end": v(-15, -104.25) * mm});
            skLineSegment(sketch, "E91.MirrorCS", {"start": v(-15, -92.25) * mm, "end": v(-33, -74.25) * mm});
            skCircle(sketch, "E92.MirrorC", {"center": v(0, -104.25) * mm, "radius": 6 * mm});
            skLineSegment(sketch, "E93.MirrorCS", {"start": v(15, -92.25) * mm, "end": v(33, -74.25) * mm});
            skSolve(sketch);
        }
        {
            var Q0;
            Q0=makeQuery(id+"F16.imprint","IMPRINT",FACE,{"disambiguationData":[TD([[makeQuery(id+"F16.imprint","IMPRINT",EDGE,{"derivedFrom":sQuery(id+"F16.wireOp",EDGE,"E80")}),1.0]])]});
            var Q1;
            Q1=makeQuery(id+"F16.imprint","IMPRINT",FACE,{"disambiguationData":[TD([[makeQuery(id+"F16.imprint","IMPRINT",EDGE,{"derivedFrom":sQuery(id+"F16.wireOp",EDGE,"E87.MirrorCS")}),1.0]])]});
            var Q2;
            Q2=makeQuery(id+"F16.imprint","IMPRINT",FACE,{"disambiguationData":[TD([[makeQuery(id+"F16.imprint","IMPRINT",EDGE,{"derivedFrom":makeQuery(id+"F1.opExtrude","CAP_EDGE",EDGE,{"disambiguationData":[OSD([sQuery(id+"F0.wireOp",EDGE,"E1.left")])],"isStart":true})}),-1.0]])]});
            var Q3;
            Q3=makeQuery(id+"F2.opExtrude","CAP_FACE",FACE,{"disambiguationData":[OSD([sQuery(id+"F0.wireOp",EDGE,"E12"),sQuery(id+"F0.wireOp",EDGE,"E13"),sQuery(id+"F0.wireOp",EDGE,"E14"),sQuery(id+"F0.wireOp",EDGE,"E15"),sQuery(id+"F0.wireOp",EDGE,"E17.filletArc"),sQuery(id+"F0.wireOp",EDGE,"E18.filletArc"),sQuery(id+"F0.wireOp",EDGE,"E19.filletArc"),sQuery(id+"F0.wireOp",EDGE,"E20.filletArc"),sQuery(id+"F0.wireOp",EDGE,"E25.0"),sQuery(id+"F0.wireOp",EDGE,"E25.1"),sQuery(id+"F0.wireOp",EDGE,"E25.2"),sQuery(id+"F0.wireOp",EDGE,"E25.3"),sQuery(id+"F0.wireOp",EDGE,"E25.4"),sQuery(id+"F0.wireOp",EDGE,"E25.5"),sQuery(id+"F0.wireOp",EDGE,"E25.6"),sQuery(id+"F0.wireOp",EDGE,"E25.7")])],"isStart":false});
            extrude(context, id + "F17", {"entities" : qUnion([Q0, Q1, Q2]), "endBound" : BoundingType.UP_TO_SURFACE, "endBoundEntityFace" : qUnion([Q3]), "depth" : 25 * mm});
        }
    });
